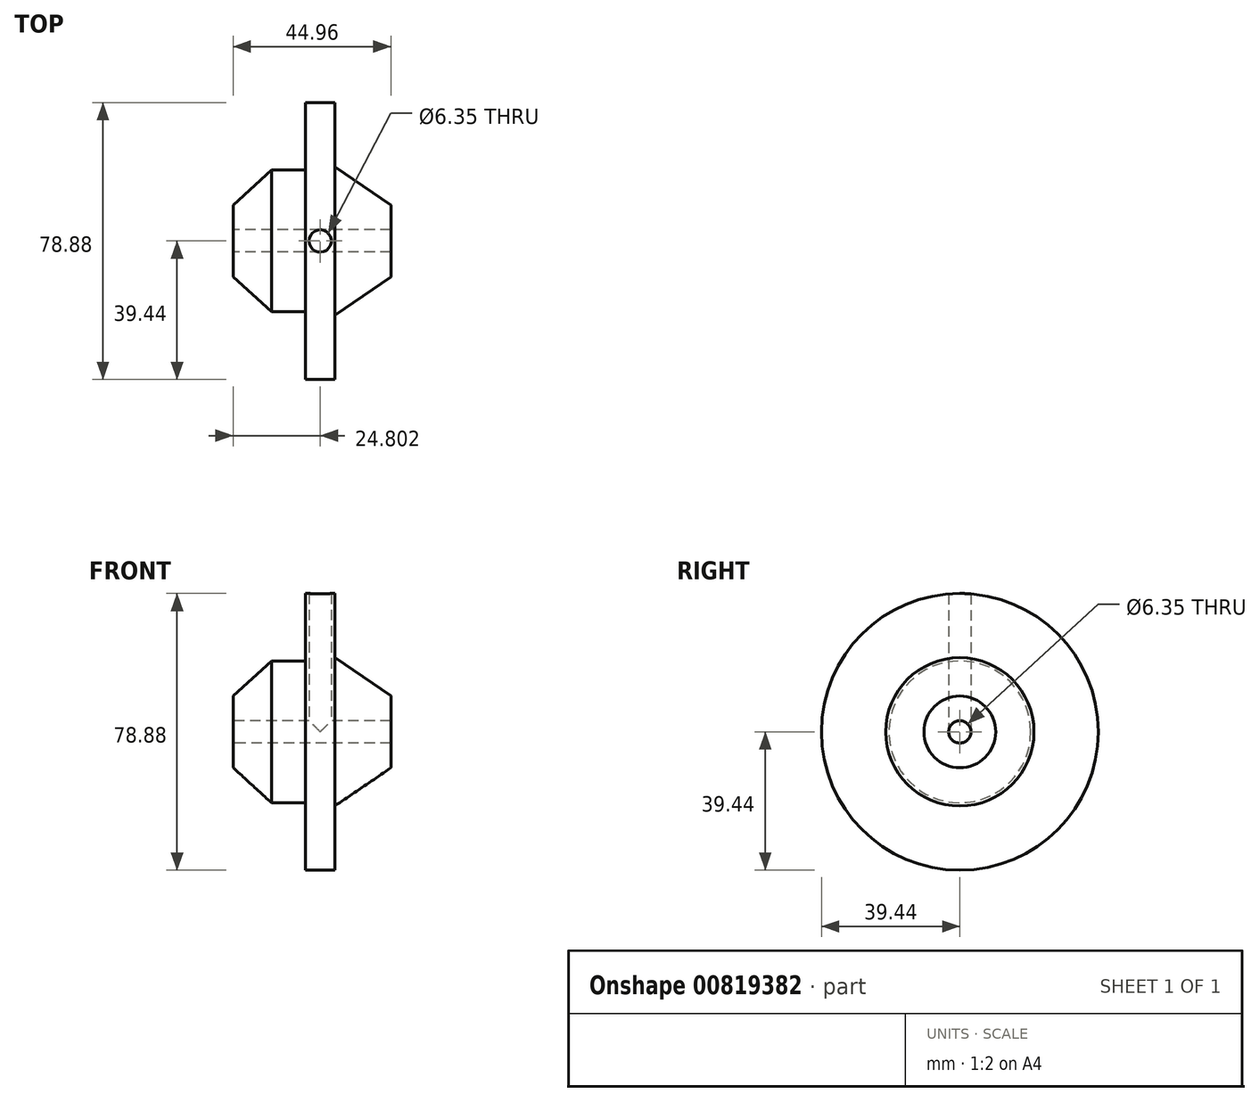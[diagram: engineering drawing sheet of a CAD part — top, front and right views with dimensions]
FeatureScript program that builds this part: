
annotation { "Feature Type Name" : "Feature", "Feature Type Description" : "" }
export const myFeature = defineFeature(function(context is Context, id is Id, definition is map)
    precondition{}
    {
        {
            var Q0;
            Q0=qCreatedBy(makeId("Front.planeOp"),FACE);
            var sketch = newSketch(context, id + "F0", { "sketchPlane" : qUnion([Q0])});
            skLineSegment(sketch, "E0", {"start": v(11, 0) * mm, "end": v(11, 10.24) * mm});
            skLineSegment(sketch, "E1", {"start": v(11, 10.24) * mm, "end": v(21.88, 20.2) * mm});
            skLineSegment(sketch, "E2", {"start": v(21.88, 20.2) * mm, "end": v(31.62, 20.2) * mm});
            skLineSegment(sketch, "E3", {"start": v(31.62, 20.2) * mm, "end": v(31.62, 39.44) * mm});
            skLineSegment(sketch, "E4", {"start": v(31.62, 39.44) * mm, "end": v(39.96, 39.44) * mm});
            skLineSegment(sketch, "E5", {"start": v(39.96, 39.44) * mm, "end": v(39.96, 20.2) * mm});
            skLineSegment(sketch, "E6", {"start": v(39.96, 20.2) * mm, "end": v(39.96, 21.13) * mm});
            skLineSegment(sketch, "E7", {"start": v(39.96, 21.13) * mm, "end": v(55.95, 10.24) * mm});
            skLineSegment(sketch, "E8", {"start": v(55.95, 10.24) * mm, "end": v(55.95, 0) * mm});
            skLineSegment(sketch, "E9", {"start": v(55.95, 0) * mm, "end": v(11, 0) * mm});
            skSolve(sketch);
        }
        {
            var Q0;
            Q0=makeQuery(id+"F0.imprint","IMPRINT",FACE,{"disambiguationData":[TD([[makeQuery(id+"F0.imprint","IMPRINT",EDGE,{"derivedFrom":sQuery(id+"F0.wireOp",EDGE,"E0")}),-1.0]])]});
            var Q1;
            Q1=sQuery(id+"F0.wireOp",EDGE,"E9");
            revolve(context, id + "F1", {"surfaceOperationType" : NewSurfaceOperationType.NEW, "entities" : qUnion([Q0]), "axis" : qUnion([Q1]), "revolveType" : RevolveType.FULL});
        }
        {
            var Q0;
            Q0=qCreatedBy(makeId("Right.planeOp"),FACE);
            var sketch = newSketch(context, id + "F2", { "sketchPlane" : qUnion([Q0])});
            skCircle(sketch, "E10", {"center": v(0, 0) * mm, "radius": 5.45 * mm});
            skSolve(sketch);
        }
        {
            var Q0;
            Q0=qCreatedBy(makeId("Top.planeOp"),FACE);
            var sketch = newSketch(context, id + "F3", { "sketchPlane" : qUnion([Q0])});
            skCircle(sketch, "E11", {"center": v(35.8, 0) * mm, "radius": 2.34 * mm});
            skSolve(sketch);
        }
        {
            var Q0;
            Q0=sQuery(id+"F3.wireOp",VERTEX,"E11.center");
            var Q1;
            Q1=makeQuery(id+"F1.opRevolve","SWEPT_BODY",BODY,{"disambiguationData":[OSD([sQuery(id+"F0.wireOp",EDGE,"E0"),sQuery(id+"F0.wireOp",EDGE,"E1"),sQuery(id+"F0.wireOp",EDGE,"E2"),sQuery(id+"F0.wireOp",EDGE,"E3"),sQuery(id+"F0.wireOp",EDGE,"E4"),sQuery(id+"F0.wireOp",EDGE,"E5"),sQuery(id+"F0.wireOp",EDGE,"E7"),sQuery(id+"F0.wireOp",EDGE,"E8"),sQuery(id+"F0.wireOp",EDGE,"E9")])]});
            hole(context, id + "F4", {"style" : HoleStyle.SIMPLE, "endStyle" : HoleEndStyle.THROUGH, "oppositeDirection" : true, "holeDiameter" : 6.35 * mm, "majorDiameter" : 6.35 * mm, "isTappedThrough" : true, "tappedDepth" : 12.7 * mm, "tapClearance" : 3, "locations" : qUnion([Q0]), "scope" : qUnion([Q1])});
        }
        {
            var Q0;
            Q0=sQuery(id+"F2.wireOp",VERTEX,"E10.center");
            var Q1;
            Q1=makeQuery(id+"F1.opRevolve","SWEPT_BODY",BODY,{"disambiguationData":[OSD([sQuery(id+"F0.wireOp",EDGE,"E0"),sQuery(id+"F0.wireOp",EDGE,"E1"),sQuery(id+"F0.wireOp",EDGE,"E2"),sQuery(id+"F0.wireOp",EDGE,"E3"),sQuery(id+"F0.wireOp",EDGE,"E4"),sQuery(id+"F0.wireOp",EDGE,"E5"),sQuery(id+"F0.wireOp",EDGE,"E7"),sQuery(id+"F0.wireOp",EDGE,"E8"),sQuery(id+"F0.wireOp",EDGE,"E9")])]});
            hole(context, id + "F5", {"style" : HoleStyle.SIMPLE, "endStyle" : HoleEndStyle.THROUGH, "oppositeDirection" : true, "holeDiameter" : 6.35 * mm, "majorDiameter" : 6.35 * mm, "isTappedThrough" : true, "tappedDepth" : 12.7 * mm, "tapClearance" : 3, "locations" : qUnion([Q0]), "scope" : qUnion([Q1])});
        }
    });
